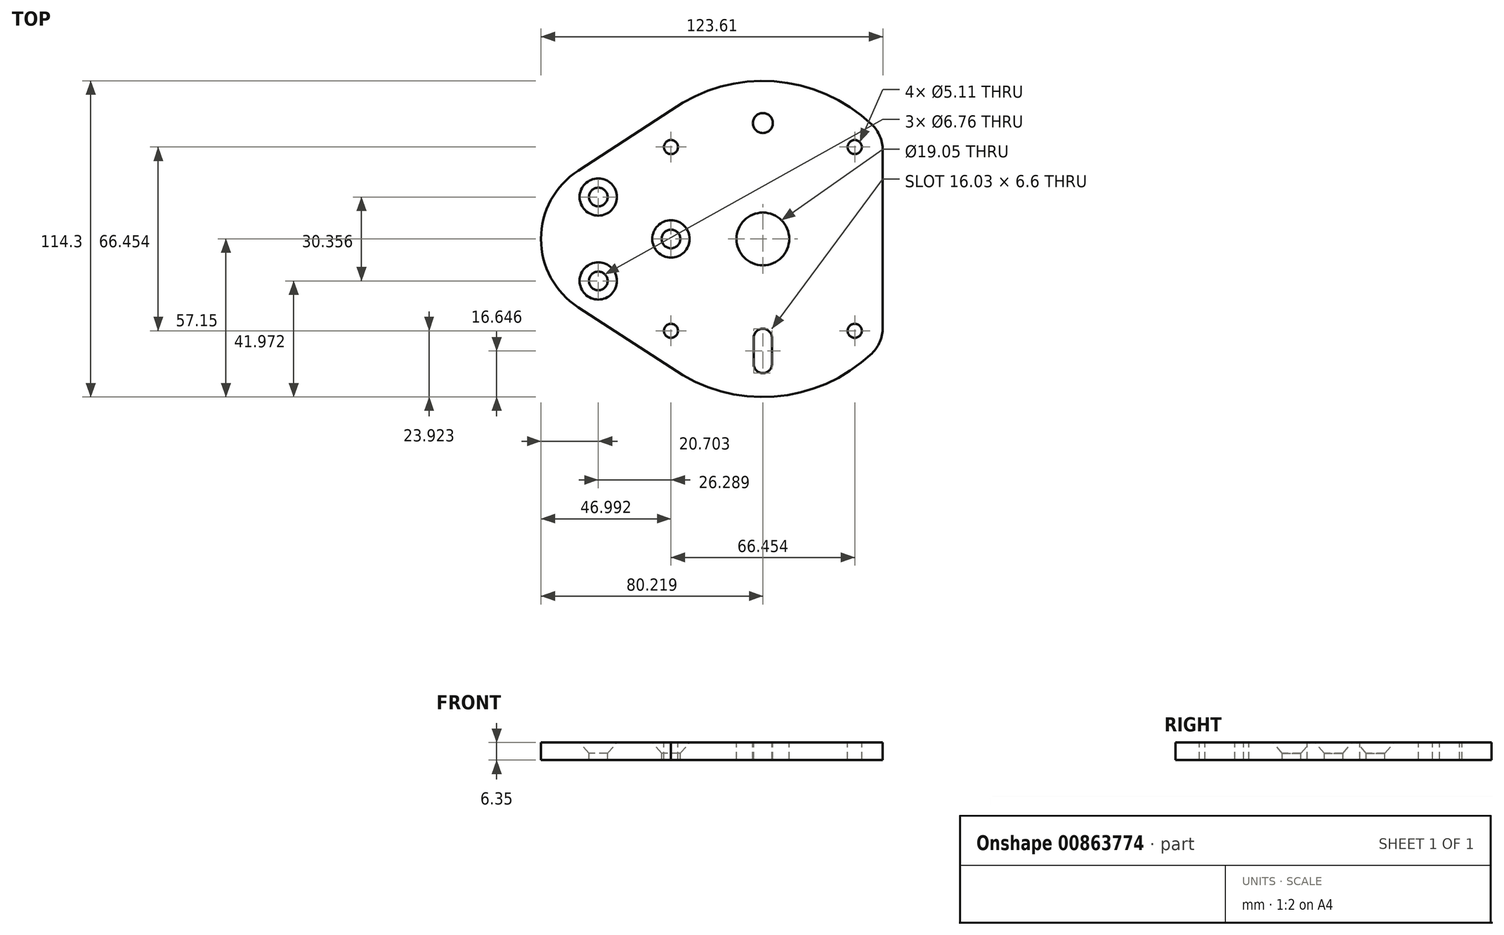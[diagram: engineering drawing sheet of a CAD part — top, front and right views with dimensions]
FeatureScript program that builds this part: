
annotation { "Feature Type Name" : "Feature", "Feature Type Description" : "" }
export const myFeature = defineFeature(function(context is Context, id is Id, definition is map)
    precondition{}
    {
        {
            var Q0;
            Q0=qCreatedBy(makeId("Top.planeOp"),FACE);
            var sketch = newSketch(context, id + "F0", { "sketchPlane" : qUnion([Q0])});
            skLineSegment(sketch, "E0", {"start": v(0, 0) * mm, "end": v(-58.93, 0) * mm, "construction": true});
            skPoint(sketch, "E1", {"position": v(-29.46, 0) * mm});
            skCircle(sketch, "E2", {"center": v(-29.46, 0) * mm, "radius": 17.53 * mm, "construction": true});
            skPoint(sketch, "E3", {"position": v(21.29, 0) * mm});
            skPoint(sketch, "E4", {"position": v(-11.94, 0) * mm});
            skCircle(sketch, "E5", {"center": v(21.29, 0) * mm, "radius": 19.05 * mm, "construction": true});
            skCircle(sketch, "E6", {"center": v(21.29, 0) * mm, "radius": 31.75 * mm, "construction": true});
            skCircle(sketch, "E7", {"center": v(54.52, 33.23) * mm, "radius": 2.55 * mm});
            skCircle(sketch, "E8", {"center": v(21.29, 0) * mm, "radius": 9.53 * mm});
            skCircle(sketch, "E9", {"center": v(21.29, 0) * mm, "radius": 35.94 * mm, "construction": true});
            skLineSegment(sketch, "E10", {"start": v(21.29, 57.15) * mm, "end": v(21.29, -57.15) * mm, "construction": true});
            skCircle(sketch, "E11", {"center": v(21.29, 0) * mm, "radius": 45.34 * mm, "construction": true});
            skLineSegment(sketch, "E12", {"start": v(21.29, 0) * mm, "end": v(61.7, 40.41) * mm, "construction": true});
            skCircle(sketch, "E13", {"center": v(21.29, 0) * mm, "radius": 46.99 * mm, "construction": true});
            skCircle(sketch, "E14.1.0", {"center": v(-11.94, 33.23) * mm, "radius": 2.55 * mm});
            skCircle(sketch, "E14.2.0", {"center": v(-11.94, -33.23) * mm, "radius": 2.55 * mm});
            skCircle(sketch, "E14.3.0", {"center": v(54.52, -33.23) * mm, "radius": 2.55 * mm});
            skLineSegment(sketch, "E15", {"start": v(21.29, 0) * mm, "end": v(-19.12, 40.41) * mm, "construction": true});
            skLineSegment(sketch, "E16", {"start": v(21.29, 0) * mm, "end": v(-19.12, -40.41) * mm, "construction": true});
            skCircle(sketch, "E17", {"center": v(21.29, 0) * mm, "radius": 57.15 * mm, "construction": true});
            skCircle(sketch, "E18.converted", {"center": v(-29.46, 0) * mm, "radius": 29.46 * mm, "construction": true});
            skPoint(sketch, "E19", {"position": v(78.44, 0) * mm});
            skLineSegment(sketch, "E20", {"start": v(-38.23, 28.13) * mm, "end": v(-38.23, -28.13) * mm, "construction": true});
            skLineSegment(sketch, "E21", {"start": v(-11.94, -46.5) * mm, "end": v(-11.94, 46.5) * mm, "construction": true});
            skLineSegment(sketch, "E22", {"start": v(17.99, -35.79) * mm, "end": v(17.99, -45.22) * mm});
            skLineSegment(sketch, "E23", {"start": v(24.6, -35.79) * mm, "end": v(24.6, -45.22) * mm});
            skArc(sketch, "E24", {"start": v(17.99, -35.79) * mm, "mid": v(21.29, -32.49) * mm, "end": v(24.6, -35.79) * mm});
            skArc(sketch, "E25", {"start": v(17.99, -45.22) * mm, "mid": v(21.29, -48.52) * mm, "end": v(24.6, -45.22) * mm});
            skLineSegment(sketch, "E26", {"start": v(64.68, 32.16) * mm, "end": v(64.68, -18.05) * mm});
            skArc(sketch, "E27", {"start": v(60.74, 41.35) * mm, "mid": v(25.33, 57) * mm, "end": v(-11.94, 46.5) * mm});
            skArc(sketch, "E28", {"start": v(-11.94, -46.5) * mm, "mid": v(25.33, -57) * mm, "end": v(60.74, -41.35) * mm});
            skPoint(sketch, "E29.visualSharp", {"position": v(64.68, 37.2) * mm});
            skArc(sketch, "E29.filletArc", {"start": v(64.68, 32.16) * mm, "mid": v(63.65, 37.15) * mm, "end": v(60.74, 41.35) * mm});
            skPoint(sketch, "E30.visualSharp", {"position": v(64.68, -37.2) * mm});
            skArc(sketch, "E30.filletArc", {"start": v(60.74, -41.35) * mm, "mid": v(63.65, -37.15) * mm, "end": v(64.68, -32.16) * mm});
            skPoint(sketch, "E31.visualSharp", {"position": v(-38.23, 28.13) * mm});
            skPoint(sketch, "E32.visualSharp", {"position": v(-38.23, -28.13) * mm});
            skLineSegment(sketch, "E33.trimOffspring", {"start": v(64.68, -18.05) * mm, "end": v(64.68, -32.16) * mm});
            skLineSegment(sketch, "E34", {"start": v(-11.94, 46.5) * mm, "end": v(-45.5, 24.72) * mm});
            skLineSegment(sketch, "E35", {"start": v(-11.94, -46.5) * mm, "end": v(-45.5, -24.72) * mm});
            skArc(sketch, "E36", {"start": v(-45.5, 24.72) * mm, "mid": v(-58.93, 0) * mm, "end": v(-45.5, -24.72) * mm});
            skCircle(sketch, "E37", {"center": v(21.29, 41.91) * mm, "radius": 3.62 * mm});
            skPoint(sketch, "E38", {"position": v(-38.23, 15.18) * mm});
            skPoint(sketch, "E39", {"position": v(-38.23, -15.18) * mm});
            skSolve(sketch);
        }
        {
            var Q0;
            Q0=makeQuery(id+"F0.imprint","IMPRINT",FACE,{"disambiguationData":[TD([[makeQuery(id+"F0.imprint","IMPRINT",EDGE,{"derivedFrom":sQuery(id+"F0.wireOp",EDGE,"E7")}),-1.0]])]});
            extrude(context, id + "F1", {"entities" : qUnion([Q0]), "oppositeDirection" : true, "depth" : 6.35 * mm, "offsetDistance" : 25.4 * mm});
        }
        {
            var Q0;
            Q0=sQuery(id+"F0.wireOp",VERTEX,"E38");
            var Q1;
            Q1=sQuery(id+"F0.wireOp",VERTEX,"E4");
            var Q2;
            Q2=sQuery(id+"F0.wireOp",VERTEX,"E39");
            var Q3;
            Q3=makeQuery(id+"F1.opExtrude","SWEPT_BODY",BODY,{"disambiguationData":[OSD([sQuery(id+"F0.wireOp",EDGE,"E7"),sQuery(id+"F0.wireOp",EDGE,"E8"),sQuery(id+"F0.wireOp",EDGE,"E14.1.0"),sQuery(id+"F0.wireOp",EDGE,"E14.2.0"),sQuery(id+"F0.wireOp",EDGE,"E14.3.0"),sQuery(id+"F0.wireOp",EDGE,"E22"),sQuery(id+"F0.wireOp",EDGE,"E23"),sQuery(id+"F0.wireOp",EDGE,"E24"),sQuery(id+"F0.wireOp",EDGE,"E25"),sQuery(id+"F0.wireOp",EDGE,"E26"),sQuery(id+"F0.wireOp",EDGE,"E27"),sQuery(id+"F0.wireOp",EDGE,"E28"),sQuery(id+"F0.wireOp",EDGE,"E29.filletArc"),sQuery(id+"F0.wireOp",EDGE,"E30.filletArc"),sQuery(id+"F0.wireOp",EDGE,"E33.trimOffspring"),sQuery(id+"F0.wireOp",EDGE,"E34"),sQuery(id+"F0.wireOp",EDGE,"E35"),sQuery(id+"F0.wireOp",EDGE,"E36"),sQuery(id+"F0.wireOp",EDGE,"E37")])]});
            hole(context, id + "F2", {"style" : HoleStyle.C_SINK, "endStyle" : HoleEndStyle.THROUGH, "standardTappedOrClearance" : lookupTablePath({ "fit" : "Normal (ASME)", "standard" : "ANSI", "size" : "1/4", "type" : "Clearance" }), "standardBlindInLast" : lookupTablePath({ "fit" : "Free", "standard" : "ANSI", "size" : "1/4", "type" : "Clearance" }), "holeDiameter" : 6.76 * mm, "cSinkDiameter" : 13.5 * mm, "cSinkAngle" : 82 * degree, "majorDiameter" : 6.35 * mm, "isTappedThrough" : true, "tappedDepth" : 12.7 * mm, "tapClearance" : 3, "locations" : qUnion([Q0, Q1, Q2]), "scope" : qUnion([Q3])});
        }
    });
